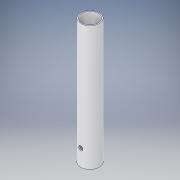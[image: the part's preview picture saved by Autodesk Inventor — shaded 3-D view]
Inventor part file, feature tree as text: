
AUTODESK INVENTOR PART (.ipt)
format: ipt  version: 2017 (Build 210142000, 142)  size: 108,032 bytes
history: native  units: in
note: dims shown in document units (in); Inventor stores cm internally (conversion verified against a paired STEP export)
features: sketch x2, extrude x1, plane x1, hole x1
ambient origin geometry x8: Origin, YZ Plane, XZ Plane, XY Plane, X Axis, Y Axis, Z Axis, Center Point
bodies: Solid1 (feature_tree)
feature tree (5):
  extrude  "Extrusion1"  Depth=4.0in
  plane  "Work Plane1"
  hole  "Hole1"  [1 undecoded]
  sketch  "Sketch1"  dims[d0=4.5in d1=4.0in]
  sketch  "Sketch2"  dims[d2=30.0in d3=0.0in d4=4.0in d5=1.0in d6=1.0in d7=0.75in d8=0.375in d9=0.25in d10=0.5635in d11=1.0in d12=0.8108in]
note: 1 required parameter value undecoded (feature->parameter linkage not recoverable at this tier; creation-order binding heuristic only, values carry confidence <= 0.55)
